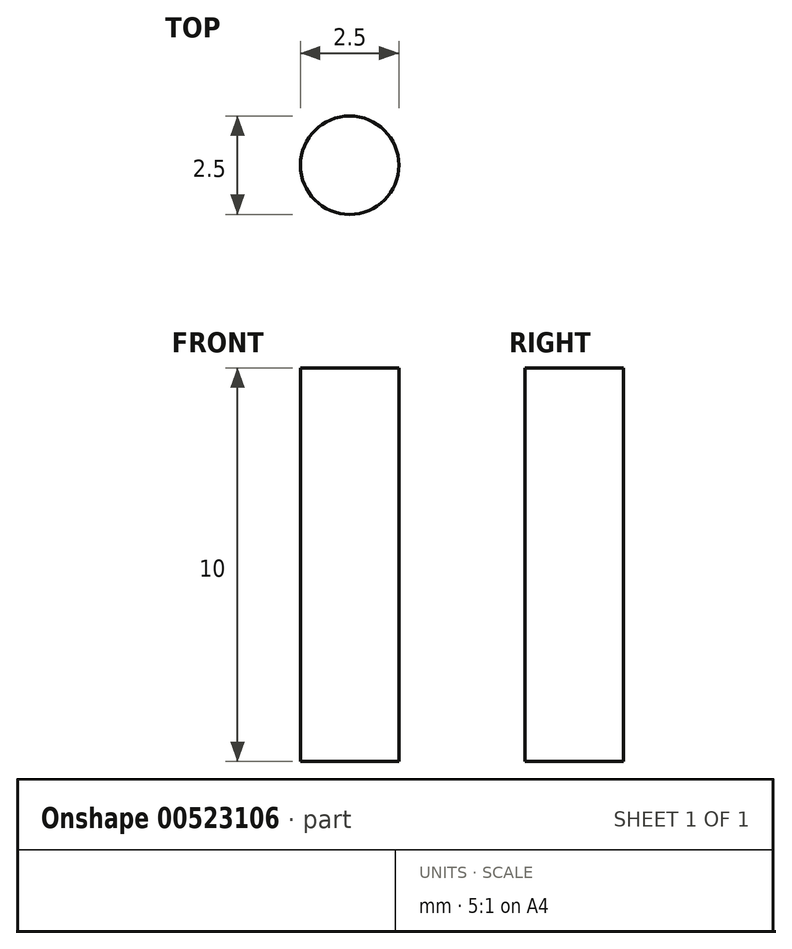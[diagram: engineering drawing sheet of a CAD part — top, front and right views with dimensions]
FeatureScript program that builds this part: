
annotation { "Feature Type Name" : "Feature", "Feature Type Description" : "" }
export const myFeature = defineFeature(function(context is Context, id is Id, definition is map)
    precondition{}
    {
        {
            var Q0;
            Q0=qCreatedBy(makeId("Top.planeOp"),FACE);
            var sketch = newSketch(context, id + "F0", { "sketchPlane" : qUnion([Q0])});
            skCircle(sketch, "E0", {"center": v(0, 0) * mm, "radius": 1.25 * mm});
            skSolve(sketch);
        }
        {
            var Q0;
            Q0 = qSketchRegion(id + "F0", true);
            extrude(context, id + "F1", {"entities" : qUnion([Q0]), "depth" : 10 * mm, "offsetDistance" : 25 * mm});
        }
    });
